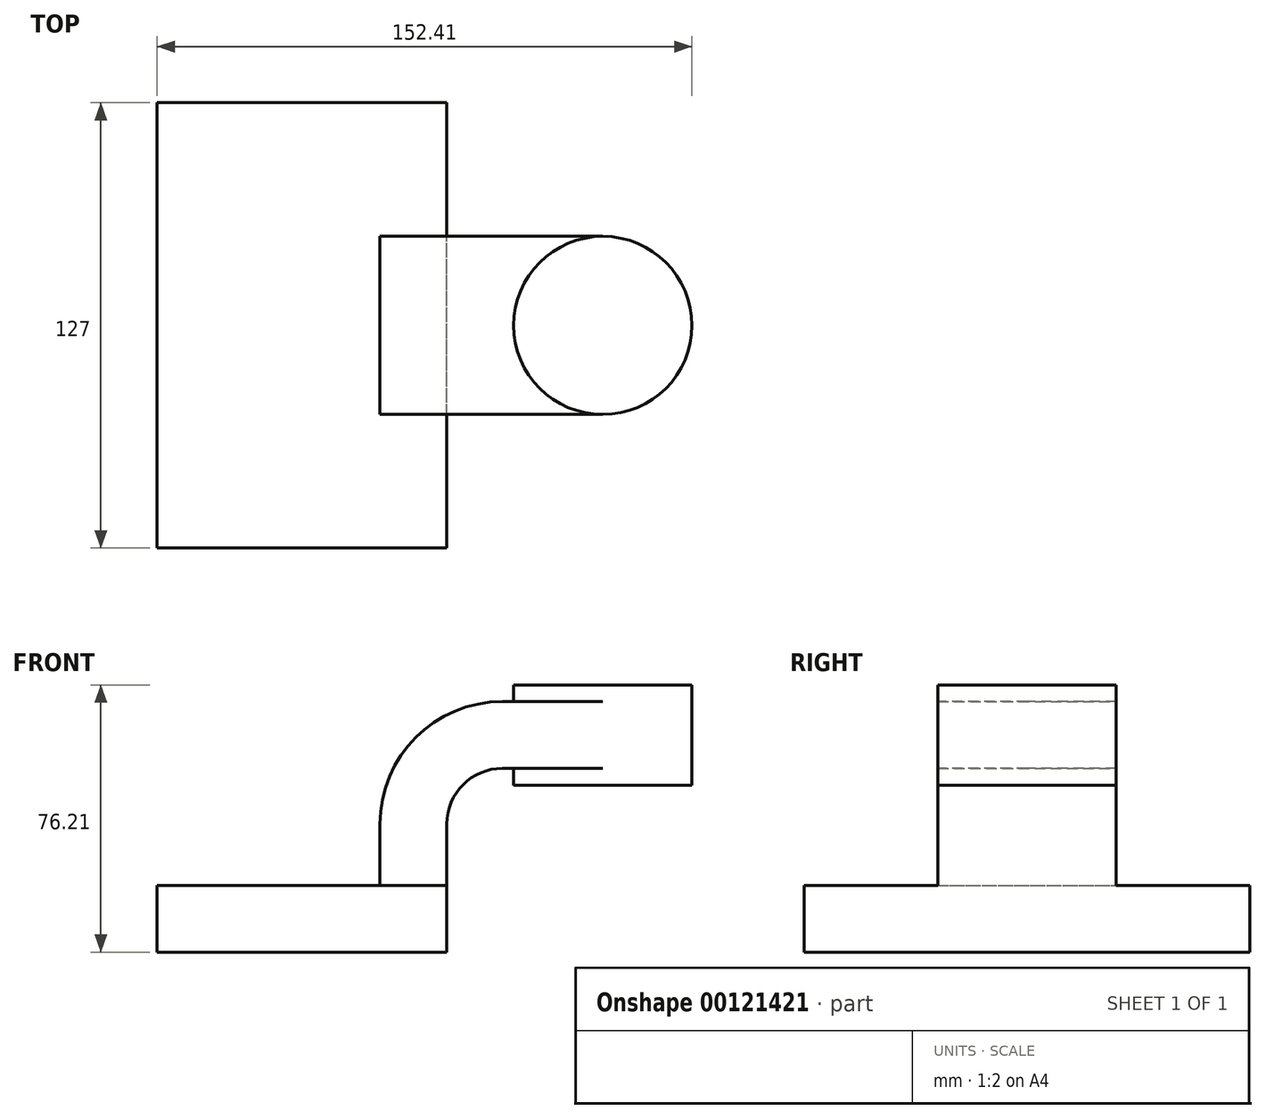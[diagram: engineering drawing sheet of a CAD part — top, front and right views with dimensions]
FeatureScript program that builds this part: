
annotation { "Feature Type Name" : "Feature", "Feature Type Description" : "" }
export const myFeature = defineFeature(function(context is Context, id is Id, definition is map)
    precondition{}
    {
        {
            var Q0;
            Q0=qCreatedBy(makeId("Front.planeOp"),FACE);
            var sketch = newSketch(context, id + "F0", { "sketchPlane" : qUnion([Q0])});
            skLineSegment(sketch, "E0.bottom", {"start": v(41.28, 9.53) * mm, "end": v(-41.28, 9.53) * mm});
            skLineSegment(sketch, "E0.top", {"start": v(41.28, -9.52) * mm, "end": v(-41.28, -9.52) * mm});
            skLineSegment(sketch, "E0.left", {"start": v(41.28, 9.53) * mm, "end": v(41.28, -9.52) * mm});
            skLineSegment(sketch, "E0.right", {"start": v(-41.28, 9.53) * mm, "end": v(-41.28, -9.52) * mm});
            skPoint(sketch, "E0.middle", {"position": v(0, 0) * mm});
            skLineSegment(sketch, "E1", {"start": v(41.28, 9.53) * mm, "end": v(41.28, 27) * mm});
            skLineSegment(sketch, "E2.bottom", {"start": v(111.13, 38.1) * mm, "end": v(60.33, 38.1) * mm});
            skLineSegment(sketch, "E2.top", {"start": v(111.13, 66.68) * mm, "end": v(60.33, 66.68) * mm});
            skLineSegment(sketch, "E2.left", {"start": v(111.13, 38.1) * mm, "end": v(111.13, 66.68) * mm});
            skLineSegment(sketch, "E2.right", {"start": v(60.33, 38.1) * mm, "end": v(60.33, 66.68) * mm});
            skPoint(sketch, "E2.middle", {"position": v(85.73, 52.39) * mm});
            skArc(sketch, "E3", {"start": v(41.27, 27) * mm, "mid": v(45.92, 38.23) * mm, "end": v(57.15, 42.88) * mm});
            skLineSegment(sketch, "E4", {"start": v(57.15, 42.88) * mm, "end": v(85.73, 42.88) * mm});
            skLineSegment(sketch, "E5.0", {"start": v(57.15, 61.93) * mm, "end": v(85.73, 61.93) * mm});
            skArc(sketch, "E5.1", {"start": v(22.22, 27) * mm, "mid": v(32.45, 51.7) * mm, "end": v(57.15, 61.93) * mm});
            skLineSegment(sketch, "E5.2", {"start": v(22.22, 9.53) * mm, "end": v(22.22, 27) * mm});
            skLineSegment(sketch, "E6", {"start": v(85.73, 42.88) * mm, "end": v(85.73, 61.93) * mm});
            skLineSegment(sketch, "E7", {"start": v(85.73, 38.1) * mm, "end": v(85.73, 66.68) * mm});
            skFitSpline(sketch, "E8", {"points": [v(-41.28, 9.52) * mm, v(57.15, 61.93) * mm], "startDerivative": vector(0, 85.73) * mm, "endDerivative": vector(121.3, 0) * mm});
            skPoint(sketch, "E9", {"position": v(-41.28, 0) * mm});
            skSolve(sketch);
        }
        {
            var Q0;
            Q0=makeQuery(id+"F0.imprint","IMPRINT",FACE,{"disambiguationData":[TD([[makeQuery(id+"F0.imprint","IMPRINT",EDGE,{"derivedFrom":sQuery(id+"F0.wireOp",EDGE,"E0.top")}),-1.0]])]});
            extrude(context, id + "F1", {"entities" : qUnion([Q0]), "endBound" : BoundingType.SYMMETRIC, "depth" : 127 * mm});
        }
        {
            var Q0;
            {var subQ6=sQuery(id+"F0.wireOp",EDGE,"E1");Q0=makeQuery(id+"F0.imprint","IMPRINT",FACE,{"disambiguationData":[TD([[makeQuery(id+"F0.imprint","IMPRINT",EDGE,{"derivedFrom":subQ6}),1.0]])]});}
            var Q1;
            {var subQ0=sQuery(id+"F0.wireOp",EDGE,"E4");var subQ1=sQuery(id+"F0.wireOp",EDGE,"E2.right");var subQ2=makeQuery(id+"F0.imprint","INTERSECT",VERTEX,{"derivedFrom":[subQ1,subQ0]});Q1=makeQuery(id+"F0.imprint","IMPRINT",FACE,{"disambiguationData":[TD([[makeQuery(id+"F0.imprint","IMPRINT",EDGE,{"disambiguationData":[TD([[subQ2,-1.0]])],"derivedFrom":subQ1}),-1.0]])]});}
            extrude(context, id + "F2", {"entities" : qUnion([Q0, Q1]), "operationType" : NewBodyOperationType.ADD, "endBound" : BoundingType.SYMMETRIC, "depth" : 50.8 * mm});
        }
        {
            var Q0;
            Q0=makeQuery(id+"F0.imprint","IMPRINT",FACE,{"disambiguationData":[TD([[makeQuery(id+"F0.imprint","IMPRINT",EDGE,{"derivedFrom":sQuery(id+"F0.wireOp",EDGE,"E5.1")}),1.0]])]});
            extrude(context, id + "F3", {"entities" : qUnion([Q0]), "operationType" : NewBodyOperationType.ADD, "endBound" : BoundingType.SYMMETRIC, "depth" : 16.5 * mm});
        }
        {
            var Q0;
            {var subQ0=sQuery(id+"F0.wireOp",EDGE,"E2.left");Q0=makeQuery(id+"F0.imprint","IMPRINT",FACE,{"disambiguationData":[TD([[makeQuery(id+"F0.imprint","IMPRINT",EDGE,{"derivedFrom":subQ0}),1.0]])]});}
            var Q1;
            Q1=sQuery(id+"F0.wireOp",EDGE,"E7");
            revolve(context, id + "F4", {"operationType" : NewBodyOperationType.ADD, "entities" : qUnion([Q0]), "axis" : qUnion([Q1]), "revolveType" : RevolveType.FULL});
        }
    });
